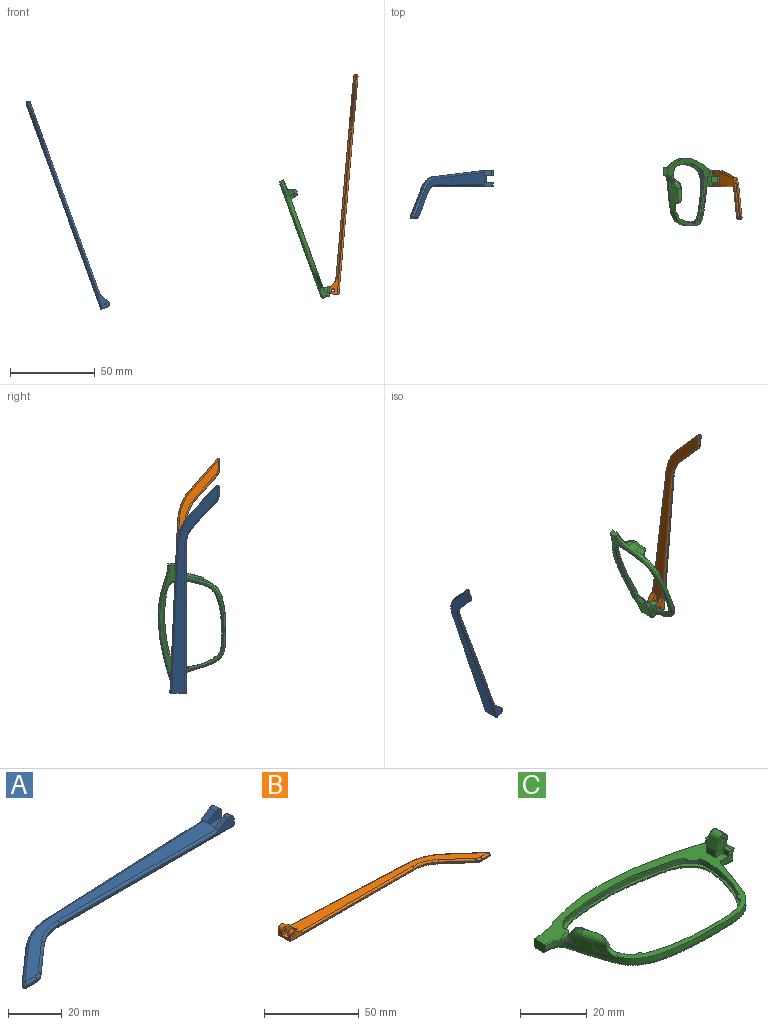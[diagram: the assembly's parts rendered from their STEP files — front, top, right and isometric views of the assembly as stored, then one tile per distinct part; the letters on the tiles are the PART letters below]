
ASSEMBLY  parts=3 mates=1
PART A: 43 faces, bbox 130.2x29.5x5.9 mm
  f0: plane 9.62x3.72mm, normal (1,0,0), area 24.7mm2, adj f1,f3,f4,f5,f10,f16,f18,f28
  f1: cylinder r=2.2mm len=3.45mm, axis (0,-1,0), area 11mm2, adj f0,f2,f4,f37
  f2: plane 6.01x3.91mm, normal (-0.55,0,0.84), area 12.7mm2, adj f1,f4,f9,f19,f37
  f3: plane 2.26x0.1mm, normal (0,0,1), area 0.1mm2, adj f0,f5,f18
  f4: plane 92.1x4.9mm, normal (0,-1,0), area 79.9mm2, adj f0,f1,f2,f14,f19,f36,f42
  f5: plane 93.42x4.13mm, normal (-0.04,1,0), area 64.8mm2, adj f0,f3,f11,f15,f17,f27,f28
  f6: plane 17.82x15.72mm, normal (-0.66,0.75,0), area 14.3mm2, adj f11,f12,f25,f30
  f7: plane 5.46x0.6mm, normal (0,-1,0), area 3.3mm2, adj f12,f13,f23,f32
  f8: plane 14.99x13.23mm, normal (0.66,-0.75,0), area 12mm2, adj f13,f14,f21,f34
  f9: plane 121.18x26.73mm, normal (0,0,1), area 627.7mm2, adj f2,f17,f19,f20,f21,f22,f23,f25
  f10: plane 129.1x27.08mm, normal (0,0,-1), area 686.5mm2, adj f0,f28,f29,f30,f32,f33,f34,f35
  f11: cylinder r=30mm len=18.52mm, axis (0,0,-1), area 12.2mm2, adj f5,f6,f26,f29
  f12: cylinder r=1mm len=1.75mm, axis (0,0,-1), area 1.5mm2, adj f6,f7,f24,f31
  f13: cylinder r=5mm len=3.31mm, axis (0,0,-1), area 2.2mm2, adj f7,f8,f22,f33
  f14: cylinder r=20mm len=13.23mm, axis (0,0,1), area 8.7mm2, adj f4,f8,f20,f35
  f15: plane 5.66x0.25mm, normal (0,0,-1), area 0.7mm2, adj f5,f17,f18
  f16: cylinder r=2.2mm len=3.45mm, axis (0,-1,0), area 14.8mm2, adj f0,f17,f18,f38
  f17: plane 6.01x3.91mm, normal (-0.55,0,0.84), area 16.9mm2, adj f5,f9,f15,f16,f18,f27,f38
  f18: plane 7.92x3.3mm, normal (0,1,0), area 15.9mm2, adj f0,f3,f15,f16,f17,f41
  f19: cylinder r=1mm len=84.18mm, axis (-1,0,0), area 131.4mm2, adj f2,f4,f9,f20
  f20: torus R=21mm, axis (0,0,1), area 23.1mm2, adj f9,f14,f19,f21
  f21: cylinder r=1mm len=15.65mm, axis (-0.75,-0.66,0), area 31.4mm2, adj f8,f9,f20,f22
  f22: torus R=4mm, axis (0,0,1), area 5.3mm2, adj f9,f13,f21,f23
  f23: cylinder r=1mm len=5.46mm, axis (-1,0,0), area 8.6mm2, adj f7,f9,f22,f24
  f24: sphere r=1mm, area 2.4mm2, adj f12,f23,f25
  f25: cylinder r=1mm len=18.48mm, axis (0.75,0.66,0), area 37.3mm2, adj f6,f9,f24,f26
  f26: torus R=29mm, axis (0,0,1), area 31.6mm2, adj f9,f11,f25,f27
  f27: cylinder r=1mm len=85.5mm, axis (1,0.04,0), area 133.5mm2, adj f5,f9,f17,f26
  f28: cylinder r=1mm len=93.46mm, axis (-1,-0.04,0), area 146.9mm2, adj f0,f5,f10,f29
  f29: torus R=29mm, axis (0,0,1), area 31.6mm2, adj f10,f11,f28,f30
  f30: cylinder r=1mm len=18.48mm, axis (-0.75,-0.66,0), area 37.3mm2, adj f6,f10,f29,f31
  f31: sphere r=1mm, area 2.4mm2, adj f12,f30,f32
  f32: cylinder r=1mm len=5.46mm, axis (1,0,0), area 8.6mm2, adj f7,f10,f31,f33
  f33: torus R=4mm, axis (0,0,1), area 5.3mm2, adj f10,f13,f32,f34
  f34: cylinder r=1mm len=15.65mm, axis (0.75,0.66,0), area 31.4mm2, adj f8,f10,f33,f35
  f35: torus R=21mm, axis (0,0,1), area 23.1mm2, adj f10,f14,f34,f36
  f36: cylinder r=1mm len=92.1mm, axis (1,0,0), area 144.7mm2, adj f0,f4,f10,f35
  f37: plane 7.92x4.7mm, normal (0,1,0), area 27mm2, adj f0,f1,f2,f39,f40,f42
  f38: plane 7.92x4.7mm, normal (0,-1,0), area 27mm2, adj f0,f16,f17,f39,f40,f41
  f39: plane 7.92x4.1mm, normal (0,0,1), area 32.5mm2, adj f0,f37,f38,f40
  f40: plane 4.1x1.4mm, normal (1,0,0), area 5.7mm2, adj f9,f37,f38,f39
  f41: cylinder r=0.5mm len=3.1mm, axis (0,-1,0), area 9.7mm2, adj f18,f38
  f42: cylinder r=0.5mm len=2.3mm, axis (0,-1,0), area 7.2mm2, adj f4,f37
PART B: 43 faces, bbox 130.2x29.5x5.9 mm
  f0: plane 9.62x3.72mm, normal (-1,0,0), area 24.7mm2, adj f1,f3,f4,f5,f10,f16,f18,f28
  f1: cylinder r=2.2mm len=3.45mm, axis (0,-1,0), area 11mm2, adj f0,f2,f4,f37
  f2: plane 6.01x3.91mm, normal (0.55,0,0.84), area 12.7mm2, adj f1,f4,f9,f19,f37
  f3: plane 2.26x0.1mm, normal (0,0,1), area 0.1mm2, adj f0,f5,f18
  f4: plane 92.1x4.9mm, normal (0,-1,0), area 78.2mm2, adj f0,f1,f2,f14,f19,f36,f42
  f5: plane 93.42x4.13mm, normal (0.04,1,0), area 64.8mm2, adj f0,f3,f11,f15,f17,f27,f28
  f6: plane 17.82x15.72mm, normal (0.66,0.75,0), area 14.3mm2, adj f11,f12,f25,f30
  f7: plane 5.46x0.6mm, normal (0,-1,0), area 3.3mm2, adj f12,f13,f23,f32
  f8: plane 14.99x13.23mm, normal (-0.66,-0.75,0), area 12mm2, adj f13,f14,f21,f34
  f9: plane 121.18x26.73mm, normal (0,0,1), area 627.7mm2, adj f2,f17,f19,f20,f21,f22,f23,f25
  f10: plane 129.1x27.08mm, normal (0,0,-1), area 686.5mm2, adj f0,f28,f29,f30,f32,f33,f34,f35
  f11: cylinder r=30mm len=18.52mm, axis (0,0,-1), area 12.2mm2, adj f5,f6,f26,f29
  f12: cylinder r=1mm len=1.75mm, axis (0,0,-1), area 1.5mm2, adj f6,f7,f24,f31
  f13: cylinder r=5mm len=3.31mm, axis (0,0,-1), area 2.2mm2, adj f7,f8,f22,f33
  f14: cylinder r=20mm len=13.23mm, axis (0,0,1), area 8.7mm2, adj f4,f8,f20,f35
  f15: plane 5.66x0.25mm, normal (0,0,-1), area 0.7mm2, adj f5,f17,f18
  f16: cylinder r=2.2mm len=3.45mm, axis (0,-1,0), area 14.8mm2, adj f0,f17,f18,f38
  f17: plane 6.01x3.91mm, normal (0.55,0,0.84), area 16.9mm2, adj f5,f9,f15,f16,f18,f27,f38
  f18: plane 7.92x3.3mm, normal (0,1,0), area 14.3mm2, adj f0,f3,f15,f16,f17,f41
  f19: cylinder r=1mm len=84.18mm, axis (1,0,0), area 131.4mm2, adj f2,f4,f9,f20
  f20: torus R=21mm, axis (0,0,1), area 23.1mm2, adj f9,f14,f19,f21
  f21: cylinder r=1mm len=15.65mm, axis (0.75,-0.66,0), area 31.4mm2, adj f8,f9,f20,f22
  f22: torus R=4mm, axis (0,0,1), area 5.3mm2, adj f9,f13,f21,f23
  f23: cylinder r=1mm len=5.46mm, axis (1,0,0), area 8.6mm2, adj f7,f9,f22,f24
  f24: sphere r=1mm, area 2.4mm2, adj f12,f23,f25
  f25: cylinder r=1mm len=18.48mm, axis (-0.75,0.66,0), area 37.3mm2, adj f6,f9,f24,f26
  f26: torus R=29mm, axis (0,0,1), area 31.6mm2, adj f9,f11,f25,f27
  f27: cylinder r=1mm len=85.5mm, axis (-1,0.04,0), area 133.5mm2, adj f5,f9,f17,f26
  f28: cylinder r=1mm len=93.46mm, axis (1,-0.04,0), area 146.9mm2, adj f0,f5,f10,f29
  f29: torus R=29mm, axis (0,0,1), area 31.6mm2, adj f10,f11,f28,f30
  f30: cylinder r=1mm len=18.48mm, axis (0.75,-0.66,0), area 37.3mm2, adj f6,f10,f29,f31
  f31: sphere r=1mm, area 2.4mm2, adj f12,f30,f32
  f32: cylinder r=1mm len=5.46mm, axis (-1,0,0), area 8.6mm2, adj f7,f10,f31,f33
  f33: torus R=4mm, axis (0,0,1), area 5.3mm2, adj f10,f13,f32,f34
  f34: cylinder r=1mm len=15.65mm, axis (-0.75,0.66,0), area 31.4mm2, adj f8,f10,f33,f35
  f35: torus R=21mm, axis (0,0,1), area 23.1mm2, adj f10,f14,f34,f36
  f36: cylinder r=1mm len=92.1mm, axis (-1,0,0), area 144.7mm2, adj f0,f4,f10,f35
  f37: plane 7.92x4.7mm, normal (0,1,0), area 25.4mm2, adj f0,f1,f2,f39,f40,f42
  f38: plane 7.92x4.7mm, normal (0,-1,0), area 25.4mm2, adj f0,f16,f17,f39,f40,f41
  f39: plane 7.92x4.1mm, normal (0,0,1), area 32.5mm2, adj f0,f37,f38,f40
  f40: plane 4.1x1.4mm, normal (-1,0,0), area 5.7mm2, adj f9,f37,f38,f39
  f41: cylinder r=0.88mm len=3.1mm, axis (0,-1,0), area 17mm2, adj f18,f38
  f42: cylinder r=0.88mm len=2.3mm, axis (0,-1,0), area 12.6mm2, adj f4,f37
PART C: 61 faces, bbox 75.1x40.9x17.9 mm
  f0: bspline ~1.82x1.22mm, area 0.7mm2, adj f2,f7,f38,f53
  f1: plane 74.08x40.46mm, normal (0,0,1), area 427.2mm2, adj f4,f5,f6,f7,f8,f9,f13,f21
  f2: bspline ~6.1x4.93mm, area 12.7mm2, adj f0,f7,f38,f42,f44,f53,f54
  f3: plane 4.46x1.45mm, normal (0,0,1), area 0.1mm2, adj f7,f39
  f4: plane 1.23x0.04mm, normal (0,0,1), area 0mm2, adj f1,f7,f23
  f5: plane 6.97x5.07mm, normal (0,1,0), area 22.7mm2, adj f1,f21,f22,f26,f28,f29,f31,f32
  f6: plane 3.2x2.36mm, normal (0,-1,0), area 5.7mm2, adj f1,f21,f27,f30
  f7: extruded ~73.26x39.84mm, area 292.7mm2, adj f0,f1,f2,f3,f4,f8,f9,f14
  f8: extruded ~35.39x5.69mm, area 72.2mm2, adj f1,f7,f9,f19
  f9: plane 4.83x3.04mm, normal (-1,0,0), area 13.9mm2, adj f1,f7,f8,f10,f14,f19,f58
  f10: plane 72.4x37.85mm, normal (0,0,-1), area 291.2mm2, adj f9,f14,f16,f18,f19,f20
  f11: plane 56.06x35.45mm, normal (0,0,1), area 127mm2, adj f12,f20
  f12: extruded ~55.69x35.36mm, area 160.5mm2, adj f11,f13
  f13: extruded ~55.69x35.36mm, area 226.3mm2, adj f1,f12,f40,f41,f42,f43,f44,f45
  f14: bspline ~73.27x30.39mm, area 161.7mm2, adj f7,f9,f10,f15
  f15: bspline ~1x1mm, area 0.8mm2, adj f7,f14,f16
  f16: bspline ~8.99x1.23mm, area 12.6mm2, adj f7,f10,f15,f17
  f17: bspline ~1.04x1mm, area 0.7mm2, adj f7,f16,f18
  f18: bspline ~45.86x8.59mm, area 59.8mm2, adj f7,f10,f17,f19
  f19: bspline ~37.01x6.7mm, area 56.6mm2, adj f8,f9,f10,f18
  f20: bspline ~56.23x35.9mm, area 235.3mm2, adj f10,f11
  f21: plane 4x2.36mm, normal (-1,0,0), area 9.5mm2, adj f1,f5,f6,f22
  f22: plane 4x0.02mm, normal (0.34,0,0.94), area 0.1mm2, adj f5,f21,f29
  f23: plane 2.76x2.53mm, normal (0,-1,0), area 3.9mm2, adj f4,f27,f28,f36,f57
  f24: plane 7.67x1.6mm, normal (0.94,0,-0.34), area 13mm2, adj f1,f36,f37,f57
  f25: plane 2.1x1.69mm, normal (0,1,0), area 2.8mm2, adj f1,f26,f28,f37,f57
  f26: plane 3.3x2.1mm, normal (-1,0,0), area 6.9mm2, adj f1,f5,f25,f28
  f27: plane 2.35x2.1mm, normal (-1,0,0), area 4.9mm2, adj f1,f6,f23,f28,f30
  f28: plane 9.65x1.24mm, normal (0,0,1), area 8.2mm2, adj f5,f23,f25,f26,f27,f30,f31,f57
  f29: plane 4x3.31mm, normal (-0.94,0,0.34), area 14.1mm2, adj f5,f22,f30,f33
  f30: plane 5.77x5.06mm, normal (0,-1,0), area 17mm2, adj f6,f27,f28,f29,f31,f32,f33,f34
  f31: plane 4x2.21mm, normal (0.94,0,-0.34), area 9.4mm2, adj f5,f28,f30,f34
  f32: plane 4x0.01mm, normal (0.34,0,0.94), area 0mm2, adj f5,f30,f33,f34
  f33: cylinder r=1.98mm len=4mm, axis (0,1,0), area 12.4mm2, adj f5,f29,f30,f32
  f34: cylinder r=1.98mm len=4mm, axis (0,-1,0), area 12.4mm2, adj f5,f30,f31,f32
  f35: cylinder r=0.88mm len=4mm, axis (0,-1,0), area 22mm2, adj f5,f30
  f36: cone r=1mm half-angle=20deg, axis (0,0,1), area 2.3mm2, adj f1,f23,f24,f57
  f37: cylinder r=1mm len=2.28mm, axis (-0.34,0,-0.94), area 3mm2, adj f1,f24,f25,f57
  f38: extruded ~3.67x3.11mm, area 5.9mm2, adj f0,f2,f7,f60
  f39: extruded ~4.44x3.32mm, area 15.1mm2, adj f3,f7,f43,f44,f56
  f40: extruded ~4.98x1.37mm, area 6.6mm2, adj f13,f42
  f41: plane 3.63x0.97mm, normal (0,0,1), area 0.3mm2, adj f13,f42,f44
  f42: bspline ~15.5x15.35mm, area 6.4mm2, adj f2,f13,f40,f41,f55
  f43: bspline ~7.26x7.26mm, area 6.3mm2, adj f13,f39,f44,f56
  f44: bspline ~10.29x4.84mm, area 21.4mm2, adj f2,f7,f13,f39,f41,f43
  f45: plane 3.19x1.37mm, normal (0,0,-1), area 2.1mm2, adj f13,f46
  f46: cylinder r=2.28mm len=3.17mm, axis (0,0,1), area 2.1mm2, adj f1,f13,f45,f55
  f47: plane 3.14x2.79mm, normal (0,0,-1), area 3.9mm2, adj f13,f48
  f48: cylinder r=2.28mm len=3.13mm, axis (0,0,1), area 2.5mm2, adj f1,f13,f47
  f49: plane 1.79x1.31mm, normal (0,0,-1), area 0.9mm2, adj f13,f50
  f50: cylinder r=1.3mm len=1.78mm, axis (0,0,1), area 1.3mm2, adj f1,f13,f49
  f51: plane 1.95x1.68mm, normal (0,0,-1), area 1.5mm2, adj f13,f52
  f52: cylinder r=1.3mm len=1.93mm, axis (0,0,1), area 1.5mm2, adj f1,f13,f51
  f53: bspline ~2.66x2.04mm, area 1.9mm2, adj f0,f2,f7,f54,f59
  f54: bspline ~3.55x3.47mm, area 3.7mm2, adj f1,f2,f53,f55,f59
  f55: bspline ~6.16x4.45mm, area 7.9mm2, adj f1,f13,f42,f46,f54
  f56: bspline ~3.7x3.66mm, area 7.8mm2, adj f1,f7,f13,f39,f43
  f57: plane 9.71x1.44mm, normal (0.34,0,0.94), area 13.9mm2, adj f23,f24,f25,f28,f36,f37
  f58: bspline ~6.38x2.14mm, area 2.6mm2, adj f1,f7,f9,f59
  f59: bspline ~2.1x1.46mm, area 0.6mm2, adj f7,f53,f54,f58
  f60: bspline ~5.24x1.75mm, area 0mm2, adj f7,f38
PLACE A rot(axis=(0,1,0),70deg) t=(-84.77,-5.75,56)mm
PLACE B rot(axis=(0,-1,0),85deg) t=(71.45,-6.11,-54.9)mm
PLACE C rot(axis=(0,1,0),70deg) t=(42.48,-1.5,73.61)mm
MATE revolute B.f41 <-> C.f34  axis (0,-1,0) through (73.34,2.35,9.23)mm
